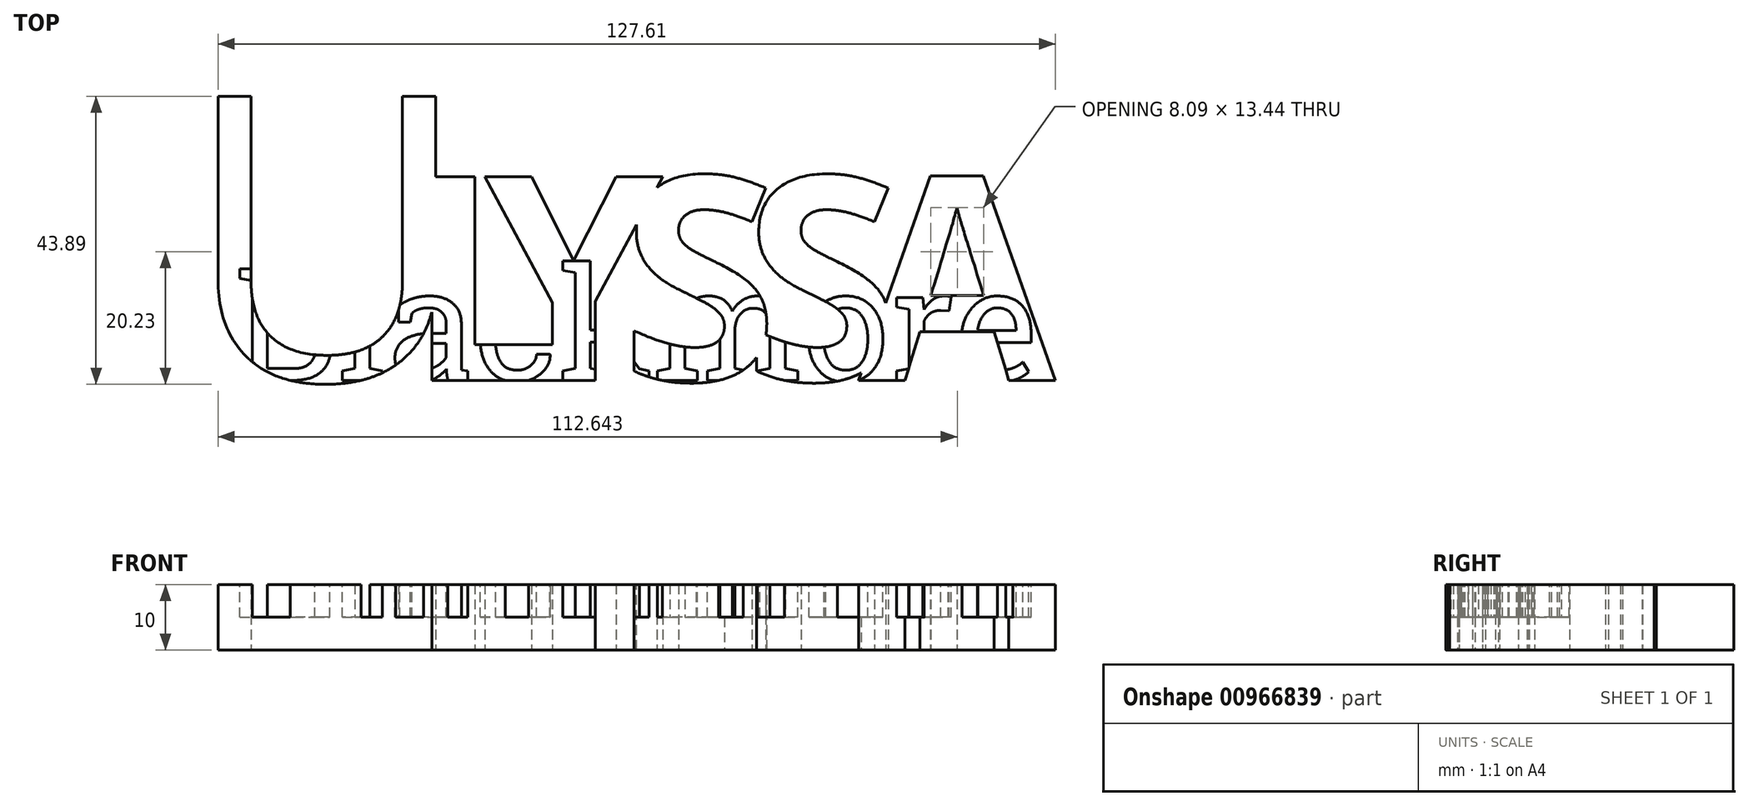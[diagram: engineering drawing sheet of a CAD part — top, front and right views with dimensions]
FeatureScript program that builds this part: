
annotation { "Feature Type Name" : "Feature", "Feature Type Description" : "" }
export const myFeature = defineFeature(function(context is Context, id is Id, definition is map)
    precondition{}
    {
        {
            var Q0;
            Q0=qCreatedBy(makeId("Top.planeOp"),FACE);
            var sketch = newSketch(context, id + "F0", { "sketchPlane" : qUnion([Q0])});
            skText(sketch, "E0", { "text": "U", "fontName": "OpenSans-Regular.ttf"});
            skText(sketch, "E1", { "text": "L", "fontName": "OpenSans-Bold.ttf"});
            skText(sketch, "E2", { "text": "Y", "fontName": "OpenSans-Bold.ttf"});
            skText(sketch, "E3", { "text": "S", "fontName": "OpenSans-Bold.ttf"});
            skText(sketch, "E4", { "text": "S", "fontName": "OpenSans-Bold.ttf"});
            skText(sketch, "E5", { "text": "A", "fontName": "OpenSans-Bold.ttf"});
            const initialGuessF0  = {"E0": [-0.09324, 0, 1, 0, 0.04366], "E1": [-0.05907, 0, 1, 0, 0.03131], "E2": [-0.04711, 0, 1, 0, 0.03131], "E3": [-0.02635, 0, 1, 0, 0.03131], "E4": [-0.0077, 0, 1, 0, 0.03131], "E5": [0.00986, 0, 1, 0, 0.03131]};
            skSetInitialGuess(sketch, initialGuessF0);
            skSolve(sketch);
        }
        {
            var Q0;
            Q0 = qSketchRegion(id + "F0", true);
            extrude(context, id + "F1", {"entities" : qUnion([Q0]), "depth" : 10 * mm, "offsetDistance" : 25 * mm});
        }
        {
            var Q0;
            Q0=makeQuery(id+"F1.opExtrude","CAP_FACE",FACE,{"disambiguationData":[OSD([sQuery(id+"F0.wireOp",EDGE,"E0.sketch_text.stroke-0"),sQuery(id+"F0.wireOp",EDGE,"E0.sketch_text.stroke-1"),sQuery(id+"F0.wireOp",EDGE,"E0.sketch_text.stroke-2"),sQuery(id+"F0.wireOp",EDGE,"E0.sketch_text.stroke-3"),sQuery(id+"F0.wireOp",EDGE,"E0.sketch_text.stroke-4"),sQuery(id+"F0.wireOp",EDGE,"E0.sketch_text.stroke-5"),sQuery(id+"F0.wireOp",EDGE,"E0.sketch_text.stroke-6"),sQuery(id+"F0.wireOp",EDGE,"E0.sketch_text.stroke-7"),sQuery(id+"F0.wireOp",EDGE,"E0.sketch_text.stroke-8"),sQuery(id+"F0.wireOp",EDGE,"E0.sketch_text.stroke-9"),sQuery(id+"F0.wireOp",EDGE,"E0.sketch_text.stroke-10"),sQuery(id+"F0.wireOp",EDGE,"E0.sketch_text.stroke-11"),sQuery(id+"F0.wireOp",EDGE,"E0.sketch_text.stroke-12"),sQuery(id+"F0.wireOp",EDGE,"E0.sketch_text.stroke-13"),sQuery(id+"F0.wireOp",EDGE,"E1.sketch_text.stroke-0"),sQuery(id+"F0.wireOp",EDGE,"E1.sketch_text.stroke-1"),sQuery(id+"F0.wireOp",EDGE,"E1.sketch_text.stroke-2"),sQuery(id+"F0.wireOp",EDGE,"E1.sketch_text.stroke-3"),sQuery(id+"F0.wireOp",EDGE,"E1.sketch_text.stroke-5"),sQuery(id+"F0.wireOp",EDGE,"E2.sketch_text.stroke-0"),sQuery(id+"F0.wireOp",EDGE,"E2.sketch_text.stroke-1"),sQuery(id+"F0.wireOp",EDGE,"E2.sketch_text.stroke-2"),sQuery(id+"F0.wireOp",EDGE,"E2.sketch_text.stroke-3"),sQuery(id+"F0.wireOp",EDGE,"E2.sketch_text.stroke-4"),sQuery(id+"F0.wireOp",EDGE,"E2.sketch_text.stroke-5"),sQuery(id+"F0.wireOp",EDGE,"E2.sketch_text.stroke-6"),sQuery(id+"F0.wireOp",EDGE,"E2.sketch_text.stroke-7"),sQuery(id+"F0.wireOp",EDGE,"E2.sketch_text.stroke-8"),sQuery(id+"F0.wireOp",EDGE,"E3.sketch_text.stroke-0"),sQuery(id+"F0.wireOp",EDGE,"E3.sketch_text.stroke-1"),sQuery(id+"F0.wireOp",EDGE,"E3.sketch_text.stroke-2"),sQuery(id+"F0.wireOp",EDGE,"E3.sketch_text.stroke-3"),sQuery(id+"F0.wireOp",EDGE,"E3.sketch_text.stroke-4"),sQuery(id+"F0.wireOp",EDGE,"E3.sketch_text.stroke-5"),sQuery(id+"F0.wireOp",EDGE,"E3.sketch_text.stroke-6"),sQuery(id+"F0.wireOp",EDGE,"E3.sketch_text.stroke-7"),sQuery(id+"F0.wireOp",EDGE,"E3.sketch_text.stroke-8"),sQuery(id+"F0.wireOp",EDGE,"E3.sketch_text.stroke-9"),sQuery(id+"F0.wireOp",EDGE,"E3.sketch_text.stroke-10"),sQuery(id+"F0.wireOp",EDGE,"E3.sketch_text.stroke-11"),sQuery(id+"F0.wireOp",EDGE,"E3.sketch_text.stroke-12"),sQuery(id+"F0.wireOp",EDGE,"E3.sketch_text.stroke-13"),sQuery(id+"F0.wireOp",EDGE,"E3.sketch_text.stroke-14"),sQuery(id+"F0.wireOp",EDGE,"E3.sketch_text.stroke-15"),sQuery(id+"F0.wireOp",EDGE,"E3.sketch_text.stroke-16"),sQuery(id+"F0.wireOp",EDGE,"E3.sketch_text.stroke-17"),sQuery(id+"F0.wireOp",EDGE,"E3.sketch_text.stroke-18"),sQuery(id+"F0.wireOp",EDGE,"E3.sketch_text.stroke-19"),sQuery(id+"F0.wireOp",EDGE,"E3.sketch_text.stroke-20"),sQuery(id+"F0.wireOp",EDGE,"E3.sketch_text.stroke-21"),sQuery(id+"F0.wireOp",EDGE,"E3.sketch_text.stroke-22"),sQuery(id+"F0.wireOp",EDGE,"E3.sketch_text.stroke-23"),sQuery(id+"F0.wireOp",EDGE,"E3.sketch_text.stroke-24"),sQuery(id+"F0.wireOp",EDGE,"E3.sketch_text.stroke-25"),sQuery(id+"F0.wireOp",EDGE,"E3.sketch_text.stroke-26"),sQuery(id+"F0.wireOp",EDGE,"E3.sketch_text.stroke-27"),sQuery(id+"F0.wireOp",EDGE,"E4.sketch_text.stroke-1"),sQuery(id+"F0.wireOp",EDGE,"E4.sketch_text.stroke-2"),sQuery(id+"F0.wireOp",EDGE,"E4.sketch_text.stroke-3"),sQuery(id+"F0.wireOp",EDGE,"E4.sketch_text.stroke-4"),sQuery(id+"F0.wireOp",EDGE,"E4.sketch_text.stroke-5"),sQuery(id+"F0.wireOp",EDGE,"E4.sketch_text.stroke-6"),sQuery(id+"F0.wireOp",EDGE,"E4.sketch_text.stroke-7"),sQuery(id+"F0.wireOp",EDGE,"E4.sketch_text.stroke-8"),sQuery(id+"F0.wireOp",EDGE,"E4.sketch_text.stroke-9"),sQuery(id+"F0.wireOp",EDGE,"E4.sketch_text.stroke-10"),sQuery(id+"F0.wireOp",EDGE,"E4.sketch_text.stroke-11"),sQuery(id+"F0.wireOp",EDGE,"E4.sketch_text.stroke-12"),sQuery(id+"F0.wireOp",EDGE,"E4.sketch_text.stroke-13"),sQuery(id+"F0.wireOp",EDGE,"E4.sketch_text.stroke-14"),sQuery(id+"F0.wireOp",EDGE,"E4.sketch_text.stroke-15"),sQuery(id+"F0.wireOp",EDGE,"E4.sketch_text.stroke-16"),sQuery(id+"F0.wireOp",EDGE,"E4.sketch_text.stroke-17"),sQuery(id+"F0.wireOp",EDGE,"E4.sketch_text.stroke-18"),sQuery(id+"F0.wireOp",EDGE,"E4.sketch_text.stroke-19"),sQuery(id+"F0.wireOp",EDGE,"E4.sketch_text.stroke-20"),sQuery(id+"F0.wireOp",EDGE,"E4.sketch_text.stroke-21"),sQuery(id+"F0.wireOp",EDGE,"E4.sketch_text.stroke-22"),sQuery(id+"F0.wireOp",EDGE,"E4.sketch_text.stroke-23"),sQuery(id+"F0.wireOp",EDGE,"E4.sketch_text.stroke-24"),sQuery(id+"F0.wireOp",EDGE,"E4.sketch_text.stroke-25"),sQuery(id+"F0.wireOp",EDGE,"E4.sketch_text.stroke-26"),sQuery(id+"F0.wireOp",EDGE,"E4.sketch_text.stroke-27"),sQuery(id+"F0.wireOp",EDGE,"E5.sketch_text.stroke-0"),sQuery(id+"F0.wireOp",EDGE,"E5.sketch_text.stroke-1"),sQuery(id+"F0.wireOp",EDGE,"E5.sketch_text.stroke-2"),sQuery(id+"F0.wireOp",EDGE,"E5.sketch_text.stroke-3"),sQuery(id+"F0.wireOp",EDGE,"E5.sketch_text.stroke-4"),sQuery(id+"F0.wireOp",EDGE,"E5.sketch_text.stroke-5"),sQuery(id+"F0.wireOp",EDGE,"E5.sketch_text.stroke-6"),sQuery(id+"F0.wireOp",EDGE,"E5.sketch_text.stroke-7"),sQuery(id+"F0.wireOp",EDGE,"E5.sketch_text.stroke-8"),sQuery(id+"F0.wireOp",EDGE,"E5.sketch_text.stroke-9"),sQuery(id+"F0.wireOp",EDGE,"E5.sketch_text.stroke-10"),sQuery(id+"F0.wireOp",EDGE,"E5.sketch_text.stroke-11")])],"isStart":false});
            var sketch = newSketch(context, id + "F2", { "sketchPlane" : qUnion([Q0])});
            skText(sketch, "E6", { "text": "Blackmore", "fontName": "RobotoSlab-Regular.ttf"});
            const initialGuessF2  = {"E6": [-0.08523, 0, 1, 0, 0.01722]};
            skSetInitialGuess(sketch, initialGuessF2);
            skSolve(sketch);
        }
        {
            var Q0;
            Q0 = qSketchRegion(id + "F2", true);
            extrude(context, id + "F3", {"entities" : qUnion([Q0]), "operationType" : NewBodyOperationType.REMOVE, "oppositeDirection" : true, "depth" : 5 * mm, "offsetDistance" : 25 * mm});
        }
    });
